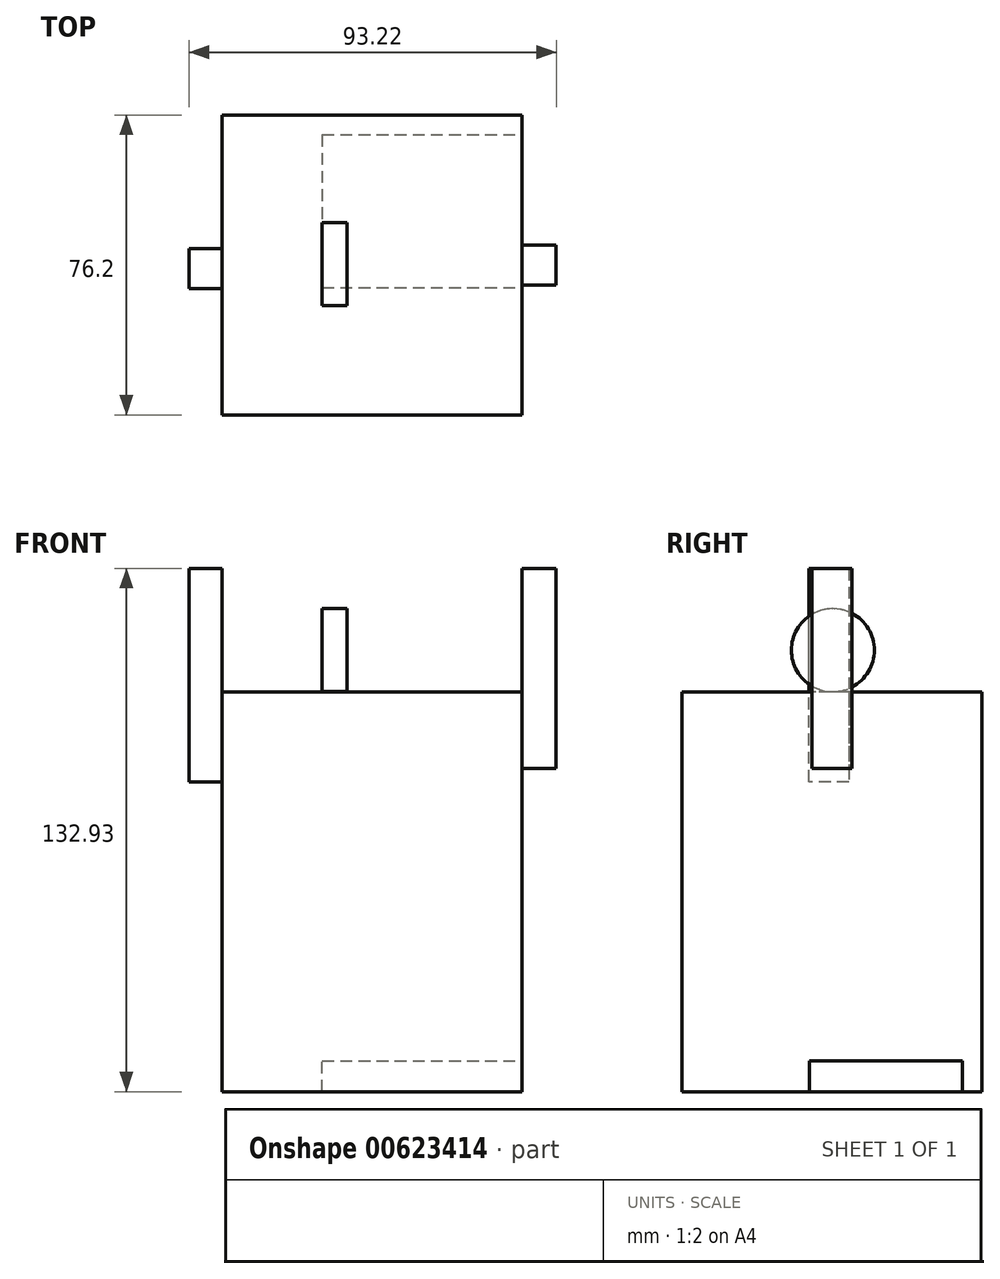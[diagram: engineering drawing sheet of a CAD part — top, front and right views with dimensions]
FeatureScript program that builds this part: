
annotation { "Feature Type Name" : "Feature", "Feature Type Description" : "" }
export const myFeature = defineFeature(function(context is Context, id is Id, definition is map)
    precondition{}
    {
        {
            var Q0;
            Q0=qCreatedBy(makeId("Front.planeOp"),FACE);
            var sketch = newSketch(context, id + "F0", { "sketchPlane" : qUnion([Q0])});
            skLineSegment(sketch, "E0", {"start": v(0, 0) * mm, "end": v(0, 101.6) * mm});
            skLineSegment(sketch, "E1", {"start": v(0, 101.6) * mm, "end": v(76.2, 101.6) * mm});
            skLineSegment(sketch, "E2", {"start": v(76.2, 101.6) * mm, "end": v(76.2, 0) * mm});
            skLineSegment(sketch, "E3", {"start": v(76.2, 0) * mm, "end": v(0, 0) * mm});
            skSolve(sketch);
        }
        {
            var Q0;
            Q0 = qSketchRegion(id + "F0", true);
            extrude(context, id + "F1", {"entities" : qUnion([Q0]), "oppositeDirection" : true, "depth" : 76.2 * mm, "offsetDistance" : 25.4 * mm});
        }
        {
            var Q0;
            Q0 = qSketchRegion(id + "F0", true);
            extrude(context, id + "F2", {"entities" : qUnion([Q0]), "operationType" : NewBodyOperationType.ADD, "oppositeDirection" : true, "depth" : 76.2 * mm, "offsetDistance" : 25.4 * mm});
        }
        {
            var Q0;
            Q0=makeQuery(id+"F1.opExtrude","SWEPT_FACE",FACE,{"disambiguationData":[OSD([sQuery(id+"F0.wireOp",EDGE,"E2")])]});
            var sketch = newSketch(context, id + "F3", { "sketchPlane" : qUnion([Q0])});
            skLineSegment(sketch, "E4", {"start": v(33.02, 132.93) * mm, "end": v(33.02, 82.13) * mm});
            skLineSegment(sketch, "E5", {"start": v(33.02, 82.13) * mm, "end": v(43.18, 82.13) * mm});
            skLineSegment(sketch, "E6", {"start": v(43.18, 82.13) * mm, "end": v(43.18, 132.93) * mm});
            skLineSegment(sketch, "E7", {"start": v(43.18, 132.93) * mm, "end": v(33.02, 132.93) * mm});
            skSolve(sketch);
        }
        {
            var Q0;
            Q0 = qSketchRegion(id + "F3", true);
            extrude(context, id + "F4", {"entities" : qUnion([Q0]), "operationType" : NewBodyOperationType.ADD, "depth" : 8.64 * mm, "offsetDistance" : 25.4 * mm});
        }
        {
            var Q0;
            Q0=makeQuery(id+"F1.opExtrude","SWEPT_FACE",FACE,{"disambiguationData":[OSD([sQuery(id+"F0.wireOp",EDGE,"E0")])]});
            var sketch = newSketch(context, id + "F5", { "sketchPlane" : qUnion([Q0])});
            skLineSegment(sketch, "E8", {"start": v(-42.33, 132.87) * mm, "end": v(-42.33, 78.75) * mm});
            skLineSegment(sketch, "E9", {"start": v(-42.33, 78.75) * mm, "end": v(-32.17, 78.75) * mm});
            skLineSegment(sketch, "E10", {"start": v(-32.17, 78.75) * mm, "end": v(-32.17, 132.87) * mm});
            skLineSegment(sketch, "E11", {"start": v(-32.17, 132.87) * mm, "end": v(-42.33, 132.87) * mm});
            skSolve(sketch);
        }
        {
            var Q0;
            Q0 = qSketchRegion(id + "F5", true);
            extrude(context, id + "F6", {"entities" : qUnion([Q0]), "operationType" : NewBodyOperationType.ADD, "depth" : 8.38 * mm, "offsetDistance" : 25.4 * mm});
        }
        {
            var Q0;
            Q0=makeQuery(id+"F1.opExtrude","SWEPT_FACE",FACE,{"disambiguationData":[OSD([sQuery(id+"F0.wireOp",EDGE,"E2")])]});
            var sketch = newSketch(context, id + "F7", { "sketchPlane" : qUnion([Q0])});
            skLineSegment(sketch, "E12.left", {"start": v(76.2, 0) * mm, "end": v(76.2, 33.05) * mm});
            skLineSegment(sketch, "E13", {"start": v(71.18, 0) * mm, "end": v(71.18, 7.76) * mm});
            skLineSegment(sketch, "E14", {"start": v(71.18, 7.76) * mm, "end": v(32.35, 7.76) * mm});
            skLineSegment(sketch, "E15", {"start": v(32.35, 7.76) * mm, "end": v(32.35, 0) * mm});
            skLineSegment(sketch, "E16", {"start": v(32.35, 0) * mm, "end": v(71.18, 0) * mm});
            skSolve(sketch);
        }
        {
            var Q0;
            Q0 = qSketchRegion(id + "F7", true);
            extrude(context, id + "F8", {"entities" : qUnion([Q0]), "operationType" : NewBodyOperationType.REMOVE, "oppositeDirection" : true, "depth" : 50.8 * mm, "offsetDistance" : 25.4 * mm});
        }
        {
            var Q0;
            Q0=qCreatedBy(makeId("Right.planeOp"),FACE);
            cPlane(context, id + "F9", {"entities" : qUnion([Q0]), "cplaneType" : CPlaneType.OFFSET, "offset" : 25.4 * mm, "width" : 152.4 * mm, "height" : 152.4 * mm});
        }
        {
            var Q0;
            Q0=qCreatedBy(id+"F9.planeOp",FACE);
            var sketch = newSketch(context, id + "F10", { "sketchPlane" : qUnion([Q0])});
            skCircle(sketch, "E17", {"center": v(38.28, 112.16) * mm, "radius": 10.54 * mm});
            skSolve(sketch);
        }
        {
            var Q0;
            Q0 = qSketchRegion(id + "F10", true);
            extrude(context, id + "F11", {"entities" : qUnion([Q0]), "operationType" : NewBodyOperationType.ADD, "depth" : 6.35 * mm, "offsetDistance" : 25.4 * mm});
        }
    });
